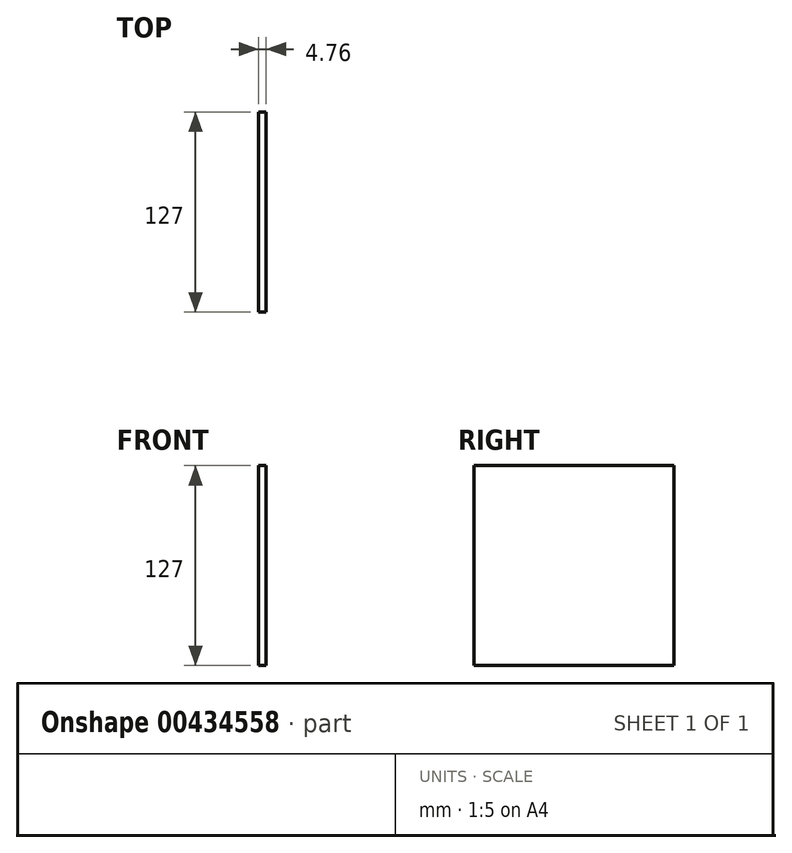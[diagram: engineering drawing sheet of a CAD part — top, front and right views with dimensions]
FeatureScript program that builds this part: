
annotation { "Feature Type Name" : "Feature", "Feature Type Description" : "" }
export const myFeature = defineFeature(function(context is Context, id is Id, definition is map)
    precondition{}
    {
        {
            var Q0;
            Q0=qCreatedBy(makeId("Right.planeOp"),FACE);
            var sketch = newSketch(context, id + "F0", { "sketchPlane" : qUnion([Q0])});
            skLineSegment(sketch, "E0.bottom", {"start": v(-58.52, 65.85) * mm, "end": v(68.48, 65.85) * mm});
            skLineSegment(sketch, "E0.top", {"start": v(-58.52, -61.15) * mm, "end": v(68.48, -61.15) * mm});
            skLineSegment(sketch, "E0.left", {"start": v(-58.52, 65.85) * mm, "end": v(-58.52, -61.15) * mm});
            skLineSegment(sketch, "E0.right", {"start": v(68.48, 65.85) * mm, "end": v(68.48, -61.15) * mm});
            skSolve(sketch);
        }
        {
            var Q0;
            Q0=makeQuery(id+"F0.imprint","IMPRINT",FACE,{"disambiguationData":[TD([[makeQuery(id+"F0.imprint","IMPRINT",EDGE,{"derivedFrom":sQuery(id+"F0.wireOp",EDGE,"E0.bottom")}),-1.0]])]});
            extrude(context, id + "F1", {"entities" : qUnion([Q0]), "depth" : 4.76 * mm});
        }
    });
